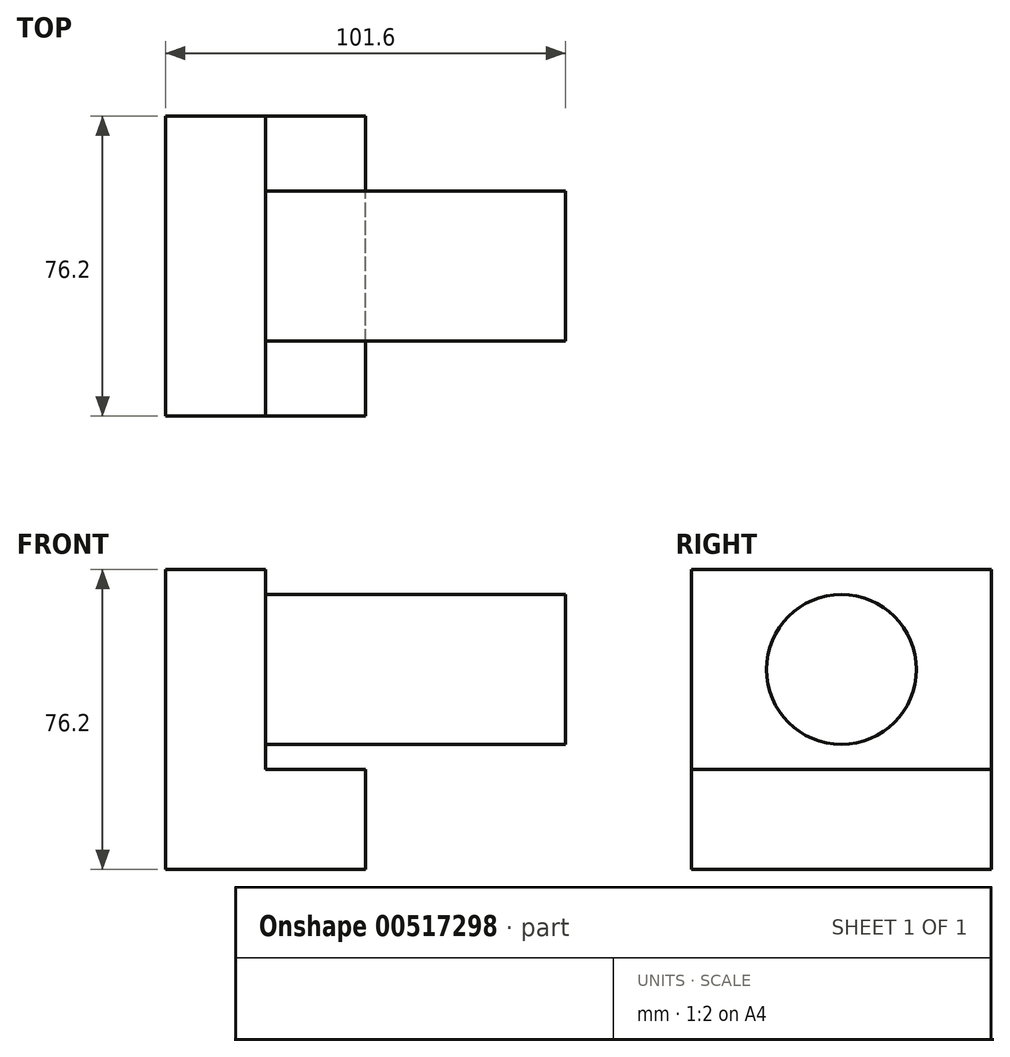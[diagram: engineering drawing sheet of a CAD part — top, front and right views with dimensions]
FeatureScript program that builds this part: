
annotation { "Feature Type Name" : "Feature", "Feature Type Description" : "" }
export const myFeature = defineFeature(function(context is Context, id is Id, definition is map)
    precondition{}
    {
        {
            var Q0;
            Q0=qCreatedBy(makeId("Front.planeOp"),FACE);
            var sketch = newSketch(context, id + "F0", { "sketchPlane" : qUnion([Q0])});
            skLineSegment(sketch, "E0", {"start": v(0, 0) * mm, "end": v(25.4, 0) * mm});
            skLineSegment(sketch, "E1", {"start": v(25.4, 0) * mm, "end": v(25.4, -25.4) * mm});
            skLineSegment(sketch, "E2", {"start": v(25.4, -25.4) * mm, "end": v(-25.4, -25.4) * mm});
            skLineSegment(sketch, "E3", {"start": v(-25.4, -25.4) * mm, "end": v(-25.4, 50.8) * mm});
            skLineSegment(sketch, "E4", {"start": v(-25.4, 50.8) * mm, "end": v(0, 50.8) * mm});
            skLineSegment(sketch, "E5", {"start": v(0, 50.8) * mm, "end": v(0, 0) * mm});
            skSolve(sketch);
        }
        {
            var Q0;
            Q0=makeQuery(id+"F0.imprint","IMPRINT",FACE,{"disambiguationData":[TD([[makeQuery(id+"F0.imprint","IMPRINT",EDGE,{"derivedFrom":sQuery(id+"F0.wireOp",EDGE,"E0")}),-1.0]])]});
            extrude(context, id + "F1", {"entities" : qUnion([Q0]), "depth" : 76.2 * mm, "offsetDistance" : 25.4 * mm});
        }
        {
            var Q0;
            Q0=makeQuery(id+"F1.opExtrude","SWEPT_FACE",FACE,{"disambiguationData":[OSD([sQuery(id+"F0.wireOp",EDGE,"E5")])]});
            var sketch = newSketch(context, id + "F2", { "sketchPlane" : qUnion([Q0])});
            skLineSegment(sketch, "E6", {"start": v(-76.2, 25.4) * mm, "end": v(0, 25.4) * mm, "construction": true});
            skLineSegment(sketch, "E7", {"start": v(-38.1, 50.8) * mm, "end": v(-38.1, 0) * mm, "construction": true});
            skCircle(sketch, "E8", {"center": v(-38.1, 25.4) * mm, "radius": 19.05 * mm});
            skSolve(sketch);
        }
        {
            var Q0;
            Q0 = qSketchRegion(id + "F2", true);
            extrude(context, id + "F3", {"entities" : qUnion([Q0]), "operationType" : NewBodyOperationType.ADD, "depth" : 76.2 * mm, "offsetDistance" : 25.4 * mm});
        }
    });
